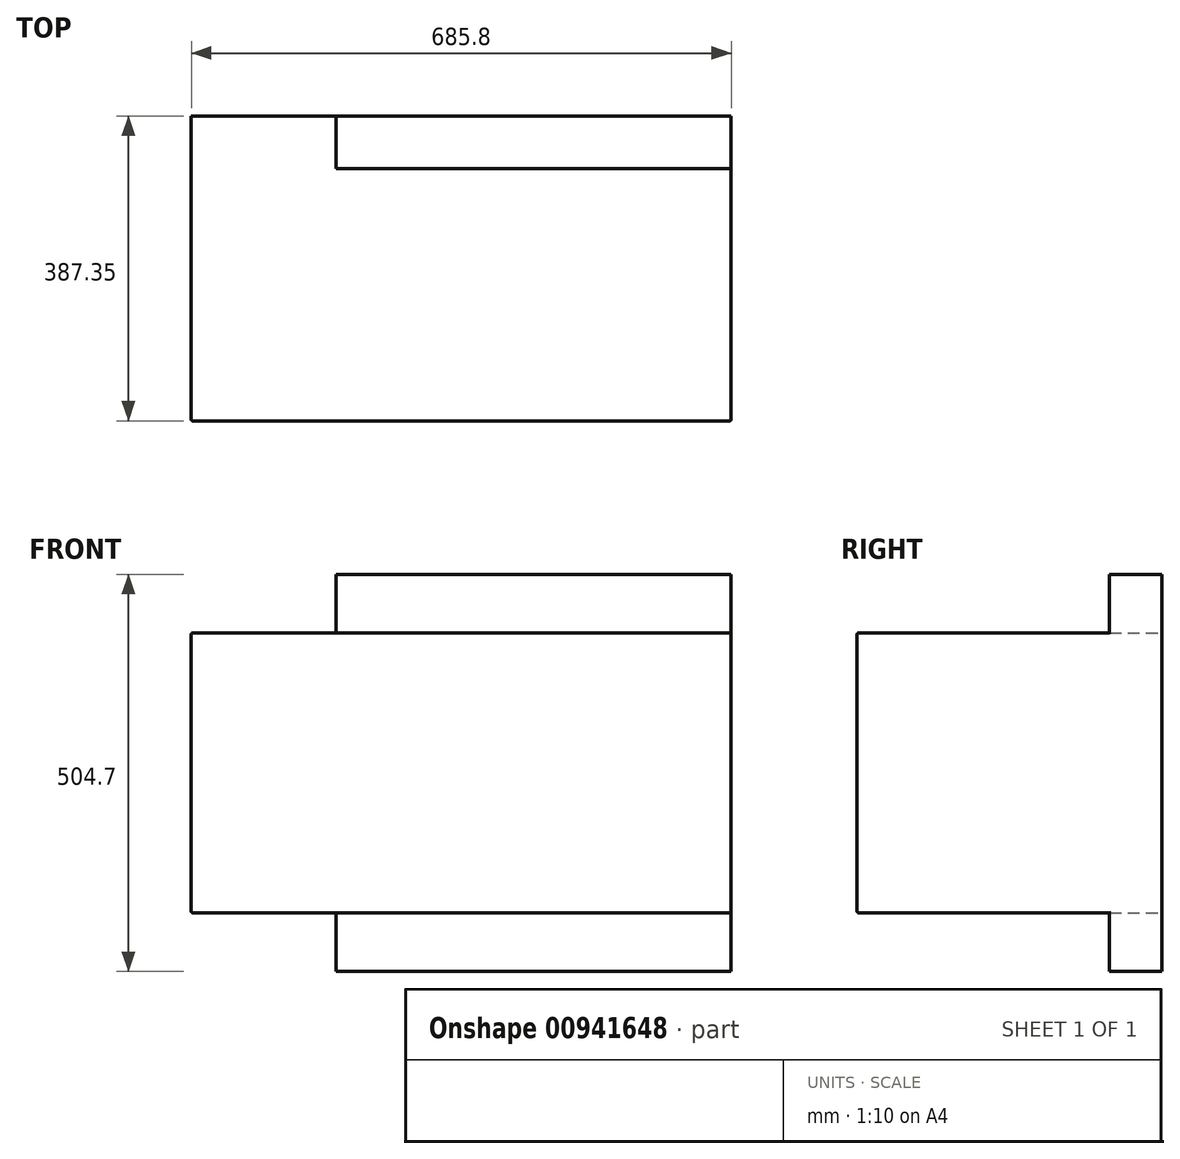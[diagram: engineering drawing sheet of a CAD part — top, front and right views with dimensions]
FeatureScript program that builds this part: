
annotation { "Feature Type Name" : "Feature", "Feature Type Description" : "" }
export const myFeature = defineFeature(function(context is Context, id is Id, definition is map)
    precondition{}
    {
        {
            var Q0;
            Q0=qCreatedBy(makeId("Front.planeOp"),FACE);
            var sketch = newSketch(context, id + "F0", { "sketchPlane" : qUnion([Q0])});
            skLineSegment(sketch, "E0.left", {"start": v(-501.24, 21.9) * mm, "end": v(-501.24, -333.7) * mm});
            skLineSegment(sketch, "E1.bottom", {"start": v(-317.1, 96.32) * mm, "end": v(184.56, 96.32) * mm});
            skLineSegment(sketch, "E1.top", {"start": v(-317.1, -408.38) * mm, "end": v(184.56, -408.38) * mm});
            skLineSegment(sketch, "E1.right", {"start": v(184.56, 96.32) * mm, "end": v(184.56, -408.38) * mm});
            skLineSegment(sketch, "E2", {"start": v(-317.1, 96.32) * mm, "end": v(-317.1, 21.9) * mm});
            skLineSegment(sketch, "E3", {"start": v(-317.1, -408.38) * mm, "end": v(-317.1, -333.7) * mm});
            skLineSegment(sketch, "E4", {"start": v(-501.24, 21.9) * mm, "end": v(-317.1, 21.9) * mm});
            skLineSegment(sketch, "E5", {"start": v(-501.24, -333.7) * mm, "end": v(-317.1, -333.7) * mm});
            skLineSegment(sketch, "E6", {"start": v(-317.1, 21.9) * mm, "end": v(184.56, 21.9) * mm});
            skLineSegment(sketch, "E7", {"start": v(-317.1, -333.7) * mm, "end": v(184.56, -333.7) * mm});
            skSolve(sketch);
        }
        {
            var Q0;
            {var subQ0=sQuery(id+"F0.wireOp",EDGE,"E1.bottom");Q0=makeQuery(id+"F0.imprint","IMPRINT",FACE,{"disambiguationData":[TD([[makeQuery(id+"F0.imprint","IMPRINT",EDGE,{"derivedFrom":subQ0}),-1.0]])]});}
            var Q1;
            Q1=makeQuery(id+"F0.imprint","IMPRINT",FACE,{"disambiguationData":[TD([[makeQuery(id+"F0.imprint","IMPRINT",EDGE,{"derivedFrom":sQuery(id+"F0.wireOp",EDGE,"E0.left")}),1.0]])]});
            var Q2;
            {var subQ0=sQuery(id+"F0.wireOp",EDGE,"E1.top");Q2=makeQuery(id+"F0.imprint","IMPRINT",FACE,{"disambiguationData":[TD([[makeQuery(id+"F0.imprint","IMPRINT",EDGE,{"derivedFrom":subQ0}),1.0]])]});}
            extrude(context, id + "F1", {"entities" : qUnion([Q0, Q1, Q2]), "depth" : 66.67 * mm, "offsetDistance" : 25.4 * mm});
        }
        {
            var Q0;
            Q0=makeQuery(id+"F0.imprint","IMPRINT",FACE,{"disambiguationData":[TD([[makeQuery(id+"F0.imprint","IMPRINT",EDGE,{"derivedFrom":sQuery(id+"F0.wireOp",EDGE,"E0.left")}),1.0]])]});
            extrude(context, id + "F2", {"entities" : qUnion([Q0]), "operationType" : NewBodyOperationType.ADD, "depth" : 387.35 * mm, "offsetDistance" : 25.4 * mm});
        }
        {
            var Q0;
            Q0=makeQuery(id+"F2.opExtrude","CAP_EDGE",EDGE,{"disambiguationData":[OSD([sQuery(id+"F0.wireOp",EDGE,"E4"),sQuery(id+"F0.wireOp",EDGE,"E6")])],"isStart":false});
            var Q1;
            {var subQ0=sQuery(id+"F0.wireOp",EDGE,"E4");var subQ1=sQuery(id+"F0.wireOp",EDGE,"E0.left");Q1=makeQuery(id+"F2.boolean.opBoolean","MERGE",EDGE,{"derivedFrom":[makeQuery(id+"F1.opExtrude","SWEPT_EDGE",EDGE,{"disambiguationData":[OSD([subQ1,subQ0])]}),makeQuery(id+"F2.opExtrude","SWEPT_EDGE",EDGE,{"disambiguationData":[OSD([subQ1,subQ0])]})]});}
            var Q2;
            Q2=makeQuery(id+"F2.opExtrude","SWEPT_EDGE",EDGE,{"disambiguationData":[OSD([sQuery(id+"F0.wireOp",EDGE,"E1.right"),sQuery(id+"F0.wireOp",EDGE,"E6")])]});
            var Q3;
            Q3=makeQuery(id+"F2.opExtrude","CAP_EDGE",EDGE,{"disambiguationData":[OSD([sQuery(id+"F0.wireOp",EDGE,"E1.right")])],"isStart":false});
            var Q4;
            Q4=makeQuery(id+"F2.opExtrude","SWEPT_EDGE",EDGE,{"disambiguationData":[OSD([sQuery(id+"F0.wireOp",EDGE,"E1.right"),sQuery(id+"F0.wireOp",EDGE,"E7")])]});
            var Q5;
            Q5=makeQuery(id+"F2.opExtrude","CAP_EDGE",EDGE,{"disambiguationData":[OSD([sQuery(id+"F0.wireOp",EDGE,"E5"),sQuery(id+"F0.wireOp",EDGE,"E7")])],"isStart":false});
            var Q6;
            Q6=makeQuery(id+"F2.opExtrude","CAP_EDGE",EDGE,{"disambiguationData":[OSD([sQuery(id+"F0.wireOp",EDGE,"E0.left")])],"isStart":false});
            var Q7;
            {var subQ0=sQuery(id+"F0.wireOp",EDGE,"E5");var subQ1=sQuery(id+"F0.wireOp",EDGE,"E0.left");Q7=makeQuery(id+"F2.boolean.opBoolean","MERGE",EDGE,{"derivedFrom":[makeQuery(id+"F1.opExtrude","SWEPT_EDGE",EDGE,{"disambiguationData":[OSD([subQ1,subQ0])]}),makeQuery(id+"F2.opExtrude","SWEPT_EDGE",EDGE,{"disambiguationData":[OSD([subQ1,subQ0])]})]});}
            fillet(context, id + "F3", {"entities" : qUnion([Q0, Q1, Q2, Q3, Q4, Q5, Q6, Q7]), "radius" : 1.59 * mm, "tangentPropagation" : true, "allowEdgeOverflow" : false});
        }
    });
